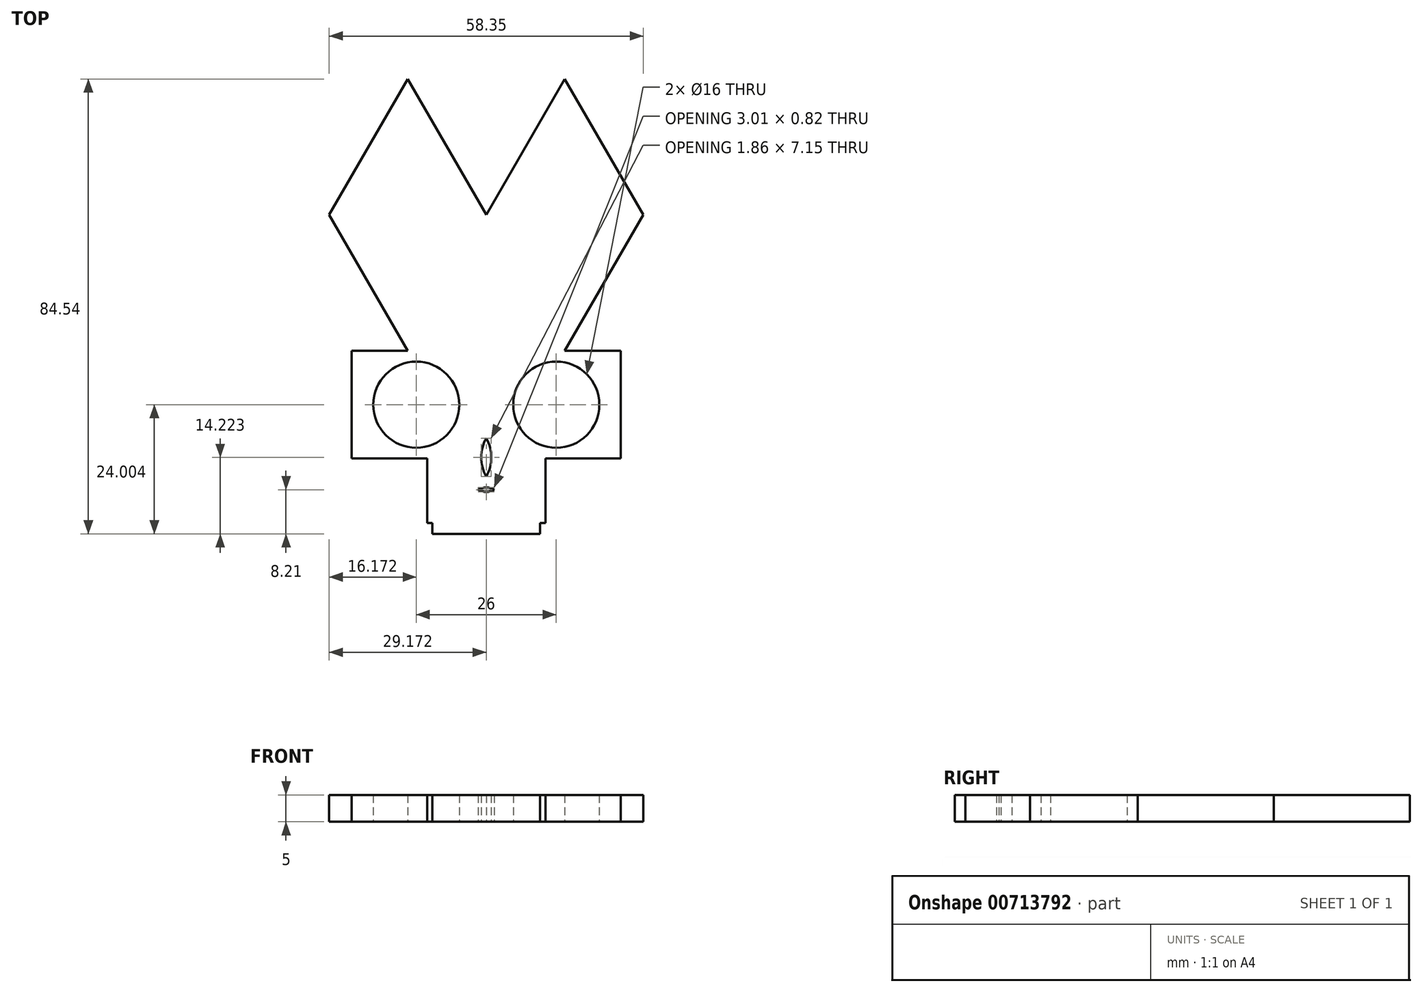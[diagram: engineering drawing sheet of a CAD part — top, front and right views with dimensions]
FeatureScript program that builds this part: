
annotation { "Feature Type Name" : "Feature", "Feature Type Description" : "" }
export const myFeature = defineFeature(function(context is Context, id is Id, definition is map)
    precondition{}
    {
        {
            var Q0;
            Q0=qCreatedBy(makeId("Top.planeOp"),FACE);
            var sketch = newSketch(context, id + "F0", { "sketchPlane" : qUnion([Q0])});
            skLineSegment(sketch, "E0.bottom", {"start": v(17.81, -25.27) * mm, "end": v(67.81, -25.27) * mm});
            skLineSegment(sketch, "E0.left", {"start": v(17.81, -25.27) * mm, "end": v(17.81, -45.27) * mm});
            skLineSegment(sketch, "E0.right", {"start": v(67.81, -25.27) * mm, "end": v(67.81, -45.27) * mm});
            skLineSegment(sketch, "E1", {"start": v(17.81, -45.27) * mm, "end": v(31.81, -45.27) * mm});
            skLineSegment(sketch, "E2.0", {"start": v(57.4, -25.27) * mm, "end": v(28.22, -25.27) * mm});
            skLineSegment(sketch, "E2.1", {"start": v(28.22, -25.27) * mm, "end": v(13.64, 0) * mm});
            skLineSegment(sketch, "E2.2", {"start": v(13.64, 0) * mm, "end": v(28.22, 25.27) * mm});
            skLineSegment(sketch, "E2.4", {"start": v(57.4, 25.27) * mm, "end": v(71.99, 0) * mm});
            skLineSegment(sketch, "E2.5", {"start": v(71.99, 0) * mm, "end": v(57.4, -25.27) * mm});
            skLineSegment(sketch, "E3", {"start": v(42.81, 0) * mm, "end": v(57.4, 25.27) * mm});
            skLineSegment(sketch, "E4", {"start": v(28.22, 25.27) * mm, "end": v(42.81, 0) * mm});
            skLineSegment(sketch, "E5.top", {"start": v(31.81, -57.27) * mm, "end": v(53.81, -57.27) * mm});
            skLineSegment(sketch, "E5.left", {"start": v(31.81, -45.27) * mm, "end": v(31.81, -57.27) * mm});
            skLineSegment(sketch, "E5.right", {"start": v(53.81, -45.27) * mm, "end": v(53.81, -57.27) * mm});
            skLineSegment(sketch, "E6", {"start": v(31.81, -57.27) * mm, "end": v(32.81, -57.27) * mm});
            skLineSegment(sketch, "E7.bottom", {"start": v(32.81, -57.27) * mm, "end": v(52.81, -57.27) * mm});
            skLineSegment(sketch, "E7.top", {"start": v(32.81, -59.27) * mm, "end": v(52.81, -59.27) * mm});
            skLineSegment(sketch, "E7.left", {"start": v(32.81, -57.27) * mm, "end": v(32.81, -59.27) * mm});
            skLineSegment(sketch, "E7.right", {"start": v(52.81, -57.27) * mm, "end": v(52.81, -59.27) * mm});
            skLineSegment(sketch, "E8.bottom", {"start": v(17.81, -25.27) * mm, "end": v(17.81, -25.27) * mm});
            skLineSegment(sketch, "E8.top", {"start": v(17.81, -35.27) * mm, "end": v(17.81, -35.27) * mm});
            skLineSegment(sketch, "E8.left", {"start": v(17.81, -25.27) * mm, "end": v(17.81, -35.27) * mm});
            skLineSegment(sketch, "E8.right", {"start": v(17.81, -25.27) * mm, "end": v(17.81, -35.27) * mm});
            skCircle(sketch, "E9", {"center": v(29.81, -35.27) * mm, "radius": 8 * mm});
            skCircle(sketch, "E10", {"center": v(55.81, -35.27) * mm, "radius": 8 * mm});
            skPoint(sketch, "E11.endSnap0", {"position": v(42.81, -45.27) * mm});
            skLineSegment(sketch, "E12", {"start": v(53.81, -45.27) * mm, "end": v(67.81, -45.27) * mm});
            skArc(sketch, "E13", {"start": v(42.81, -48.62) * mm, "mid": v(43.74, -45.05) * mm, "end": v(42.81, -41.47) * mm});
            skArc(sketch, "E14.MirrorCS", {"start": v(42.81, -48.62) * mm, "mid": v(41.88, -45.05) * mm, "end": v(42.81, -41.47) * mm});
            skArc(sketch, "E15", {"start": v(41.3, -51.06) * mm, "mid": v(42.81, -51.47) * mm, "end": v(44.32, -51.06) * mm});
            skArc(sketch, "E16.MirrorCS", {"start": v(41.3, -51.06) * mm, "mid": v(42.81, -50.65) * mm, "end": v(44.32, -51.06) * mm});
            skSolve(sketch);
        }
        {
            var Q0;
            Q0=qSketchRegion(id+"F0",true);
            extrude(context, id + "F1", {"entities" : qUnion([Q0]), "depth" : 5 * mm, "offsetDistance" : 25 * mm});
        }
    });
